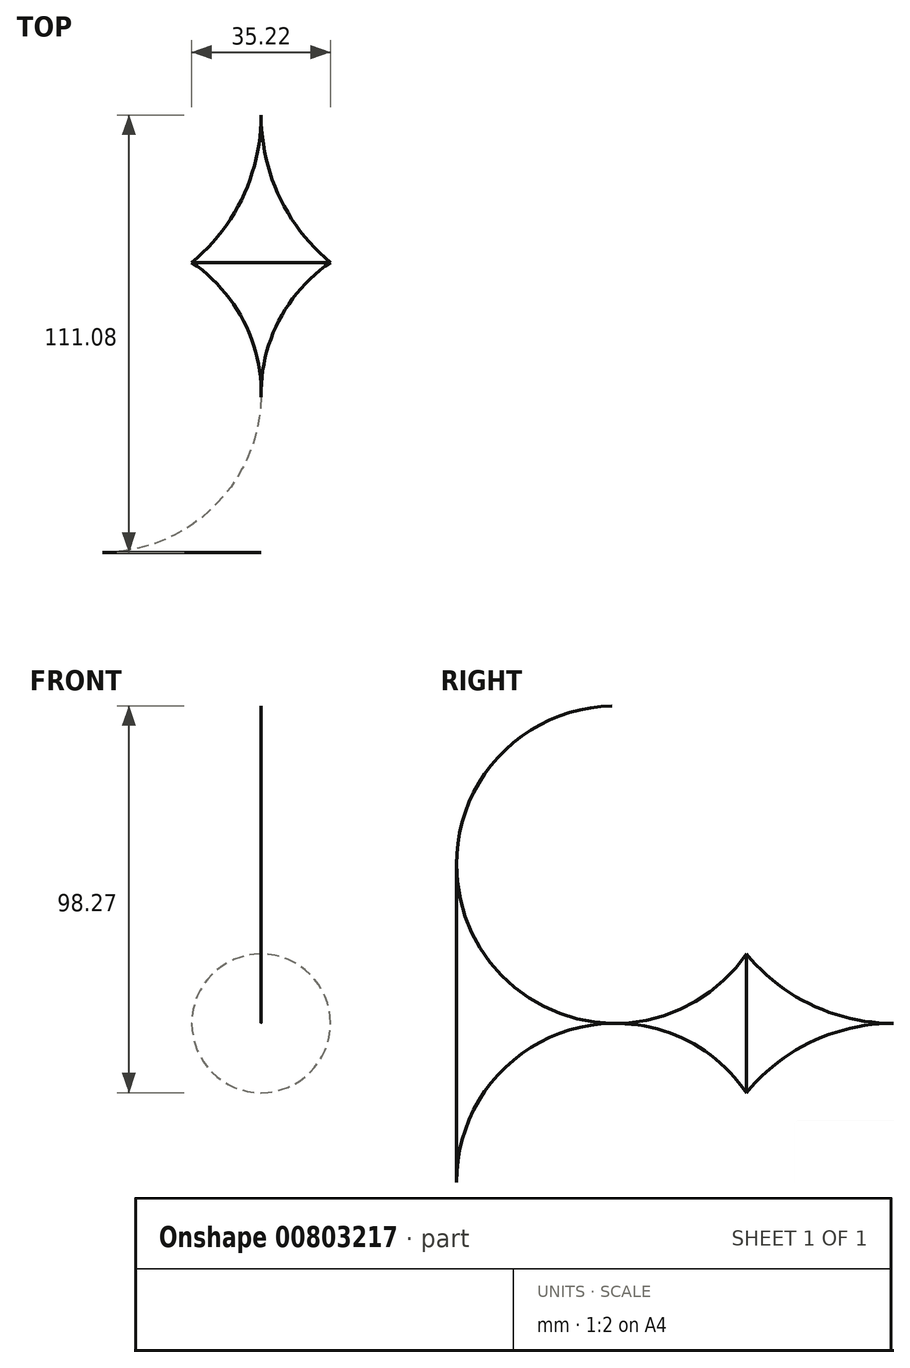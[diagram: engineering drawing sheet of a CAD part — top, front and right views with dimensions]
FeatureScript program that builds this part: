
annotation { "Feature Type Name" : "Feature", "Feature Type Description" : "" }
export const myFeature = defineFeature(function(context is Context, id is Id, definition is map)
    precondition{}
    {
        {
            var Q0;
            Q0=qCreatedBy(makeId("Top.planeOp"),FACE);
            var sketch = newSketch(context, id + "F0", { "sketchPlane" : qUnion([Q0])});
            skLineSegment(sketch, "E0", {"start": v(0, 75.56) * mm, "end": v(0, -75.37) * mm, "construction": true});
            skArc(sketch, "E1", {"start": v(17.61, 0) * mm, "mid": v(4.87, -14.1) * mm, "end": v(0, -32.49) * mm});
            skArc(sketch, "E2", {"start": v(0, 37.41) * mm, "mid": v(4.61, 16.73) * mm, "end": v(17.61, 0) * mm});
            skLineSegment(sketch, "E3", {"start": v(0, 37.41) * mm, "end": v(0, -32.49) * mm});
            skSolve(sketch);
        }
        {
            var Q0;
            {var subQ0=sQuery(id+"F0.wireOp",EDGE,"E1");Q0=makeQuery(id+"F0.imprint","IMPRINT",FACE,{"disambiguationData":[TD([[makeQuery(id+"F0.imprint","IMPRINT",EDGE,{"derivedFrom":subQ0}),-1.0]])]});}
            var Q1;
            Q1=sQuery(id+"F0.wireOp",EDGE,"E0");
            revolve(context, id + "F1", {"surfaceOperationType" : NewSurfaceOperationType.NEW, "entities" : qUnion([Q0]), "axis" : qUnion([Q1]), "revolveType" : RevolveType.FULL});
        }
    });
